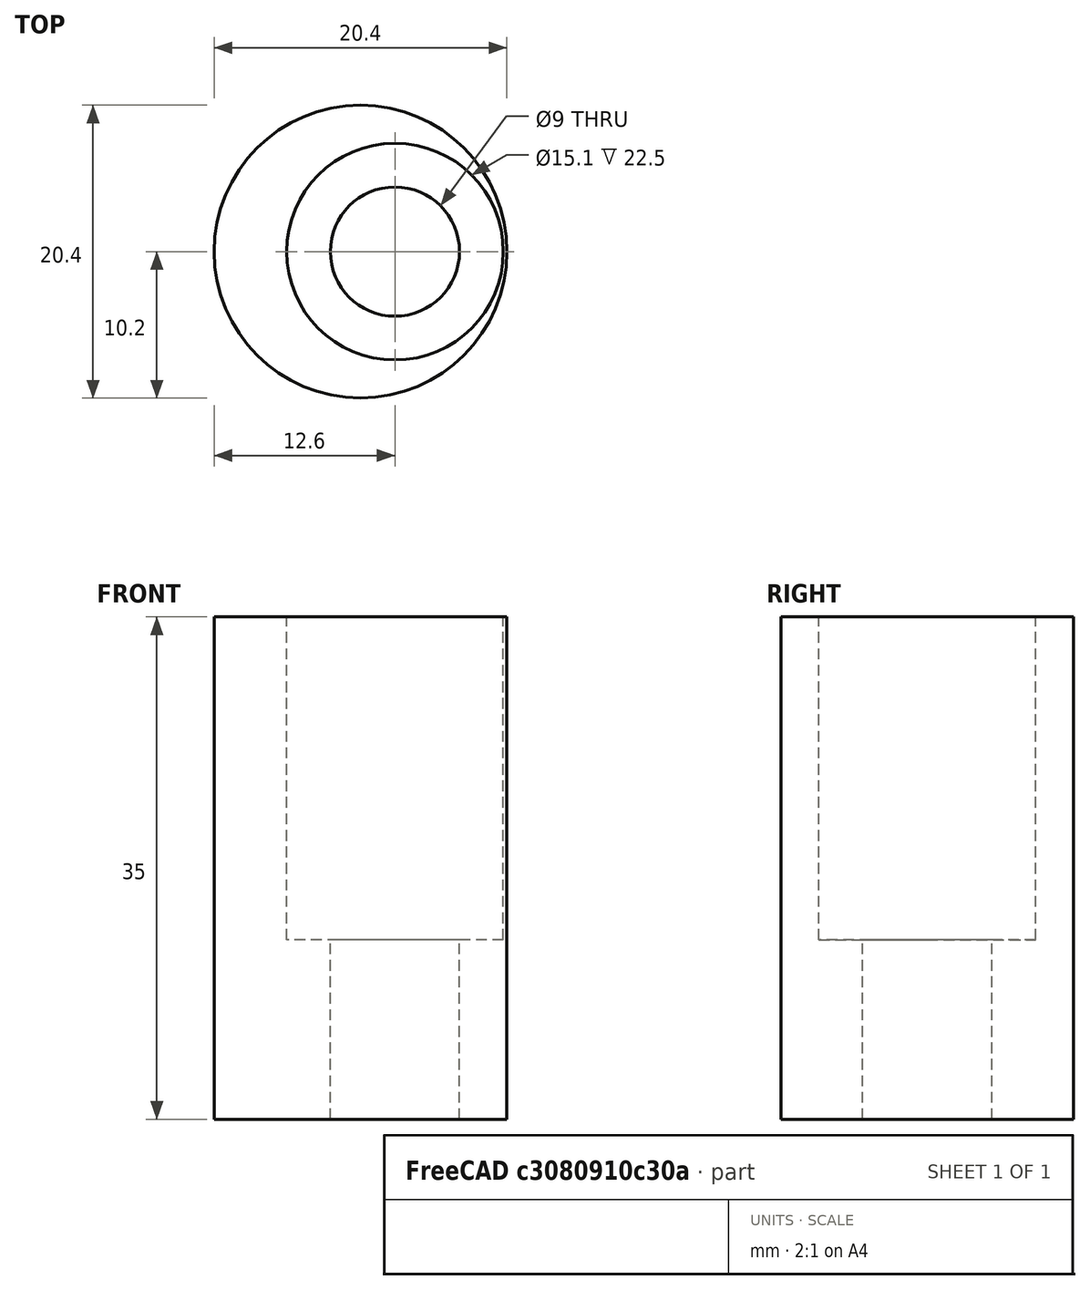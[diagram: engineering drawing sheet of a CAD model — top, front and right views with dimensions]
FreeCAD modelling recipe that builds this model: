
FCSTD DOCUMENT  (FreeCAD 0.16R6712 (Git))
Label: sujeccion_y
License: All rights reserved
LicenseURL: http://en.wikipedia.org/wiki/All_rights_reserved
objects: Part::Cylinder×7, Part::Cut×5, Part::Box×1, Part::MultiFuse×1
note: 14 computed .brp shape members not serialized (recipe doc carries the construction recipe); baked Part::Feature solids carry a one-line shape summary decoded from their .brp

FEATURE [Part::Cylinder] Cylinder  label="rodamiento"
  Angle = 360
  Height = 45
  Placement = pos=(2.4,0,12.5) rot=(0,0,1;0rad)
  Radius = 7.55
FEATURE [Part::Cylinder] Cylinder001  label="pieza_azul"
  Angle = 360
  Height = 70
  Radius = 10.2
FEATURE [Part::Cylinder] Cylinder003  label="tapa2"
  Angle = 360
  Height = 4
  Placement = pos=(0,0,66) rot=(0,0,1;0rad)
  Radius = 13
FEATURE [Part::Cylinder] Cylinder004  label="Cilindro"
  Angle = 360
  Height = 100
  Placement = pos=(2.4,0,-14) rot=(0,0,1;0rad)
  Radius = 4.5
FEATURE [Part::Box] Box  label="Cubo"
  Height = 36
  Length = 30
  Placement = pos=(-15,-15,35) rot=(0,0,1;0rad)
  Width = 30
FEATURE [Part::Cylinder] Cylinder002  label="tapa1"
  Angle = 360
  Height = 4
  Radius = 13
FEATURE [Part::MultiFuse] Fusion
  Shapes = -> [Cylinder003,Cylinder001,Cylinder002]
FEATURE [Part::Cut] Cut
  Base = -> Fusion
  Tool = -> Cylinder
FEATURE [Part::Cut] Cut001
  Base = -> Cut
  Tool = -> Cylinder004
FEATURE [Part::Cut] Cut002
  Base = -> Cut001
  Tool = -> Box
FEATURE [Part::Cylinder] Cylinder005  label="Cilindro001"
  Angle = 360
  Height = 4
  Radius = 10.2
FEATURE [Part::Cylinder] Cylinder006  label="Cilindro002"
  Angle = 360
  Height = 4
  Radius = 14
FEATURE [Part::Cut] Cut003
  Base = -> Cylinder006
  Tool = -> Cylinder005
FEATURE [Part::Cut] Cut004
  Base = -> Cut002
  Tool = -> Cut003
